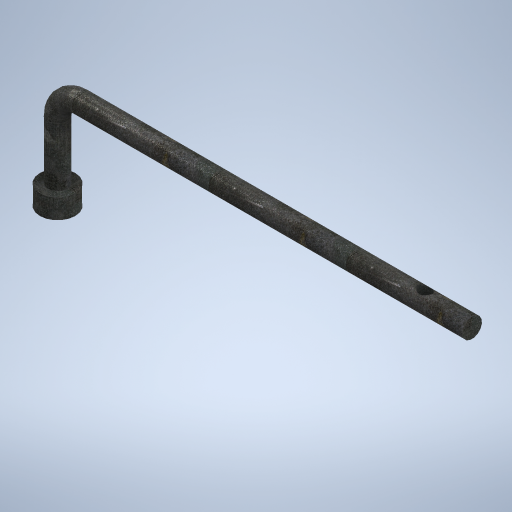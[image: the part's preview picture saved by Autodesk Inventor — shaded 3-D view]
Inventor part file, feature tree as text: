
AUTODESK INVENTOR PART (.ipt)
format: ipt  version: 2024 (Build 280153000, 153)  size: 335,872 bytes
history: native  units: mm
features: sketch x5, extrude x3, revolve x2
ambient origin geometry x8: Origin, YZ Plane, XZ Plane, XY Plane, X Axis, Y Axis, Z Axis, Center Point
bodies: Solid1 (feature_tree)
feature tree (10):
  sketch  "Sketch1"  dims[d8=25.0mm d9=500.0mm d10=0.0mm]
  extrude  "Extrusion1"  Depth=500.0mm TaperAngle=0.0deg
  extrude  "Extrusion2"  TaperAngle=90.0deg  [1 undecoded]
  revolve  "Revolution1"  [1 undecoded]
  revolve  "Revolution2"  [1 undecoded]
  extrude  "Extrusion3"  TaperAngle=90.0deg  [1 undecoded]
  sketch  "Sketch2"  dims[d11=25.0mm d12=0.0mm d13=90.0deg]
  sketch  "Sketch3"  dims[d14=30.0mm d15=75.0mm]
  sketch  "Sketch5"  dims[d16=10.0mm d17=25.0mm]
  sketch  "Sketch6"  dims[d18=22.5mm d19=90.0deg d23=90.0deg d24=120.0deg d25=21.0mm d26=120.0deg d27=120.0deg d28=0.0mm d29=120.0deg d30=0.0mm d31=10.5mm d32=10.5mm d33=20.0mm d34=0.0mm]
note: 4 required parameter values undecoded (feature->parameter linkage not recoverable at this tier; creation-order binding heuristic only, values carry confidence <= 0.55)